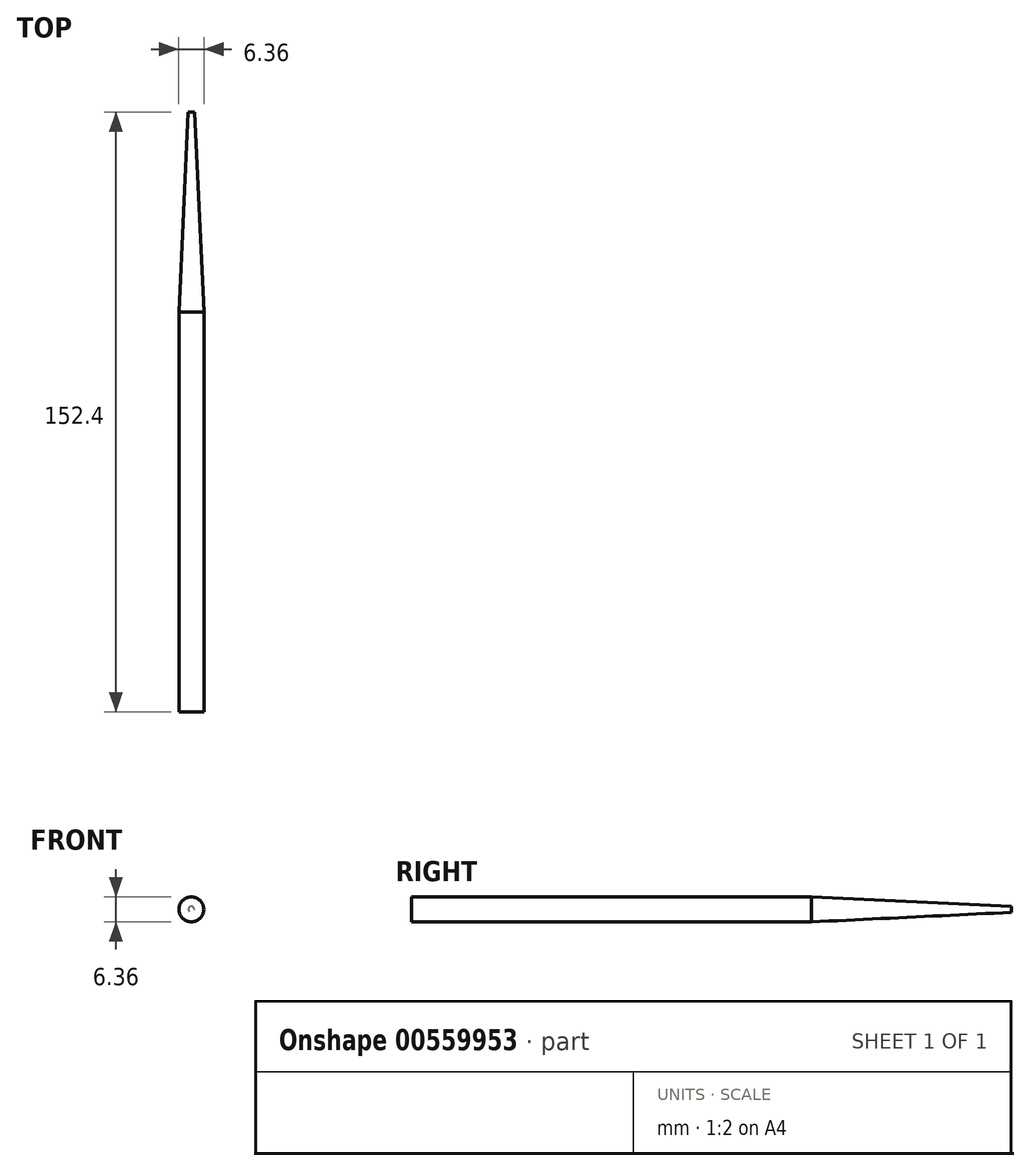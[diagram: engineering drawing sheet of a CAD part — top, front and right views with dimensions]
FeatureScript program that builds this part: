
annotation { "Feature Type Name" : "Feature", "Feature Type Description" : "" }
export const myFeature = defineFeature(function(context is Context, id is Id, definition is map)
    precondition{}
    {
        {
            var Q0;
            Q0=qCreatedBy(makeId("Right.planeOp"),FACE);
            var sketch = newSketch(context, id + "F0", { "sketchPlane" : qUnion([Q0])});
            skLineSegment(sketch, "E0", {"start": v(-55.5, 0) * mm, "end": v(67.09, 0) * mm, "construction": true});
            skLineSegment(sketch, "E1", {"start": v(50.8, 0) * mm, "end": v(50.8, 0.76) * mm});
            skLineSegment(sketch, "E2", {"start": v(50.8, 0.76) * mm, "end": v(0, 3.17) * mm});
            skLineSegment(sketch, "E3", {"start": v(-101.6, 0) * mm, "end": v(-101.6, 3.17) * mm});
            skLineSegment(sketch, "E4", {"start": v(-101.6, 0) * mm, "end": v(50.8, 0) * mm});
            skLineSegment(sketch, "E5", {"start": v(0, 3.17) * mm, "end": v(-101.6, 3.17) * mm});
            skSolve(sketch);
        }
        {
            var Q0;
            Q0 = qSketchRegion(id + "F0", true);
            var Q1;
            Q1=sQuery(id+"F0.wireOp",EDGE,"E0");
            revolve(context, id + "F1", {"entities" : qUnion([Q0]), "axis" : qUnion([Q1]), "revolveType" : RevolveType.FULL});
        }
    });
